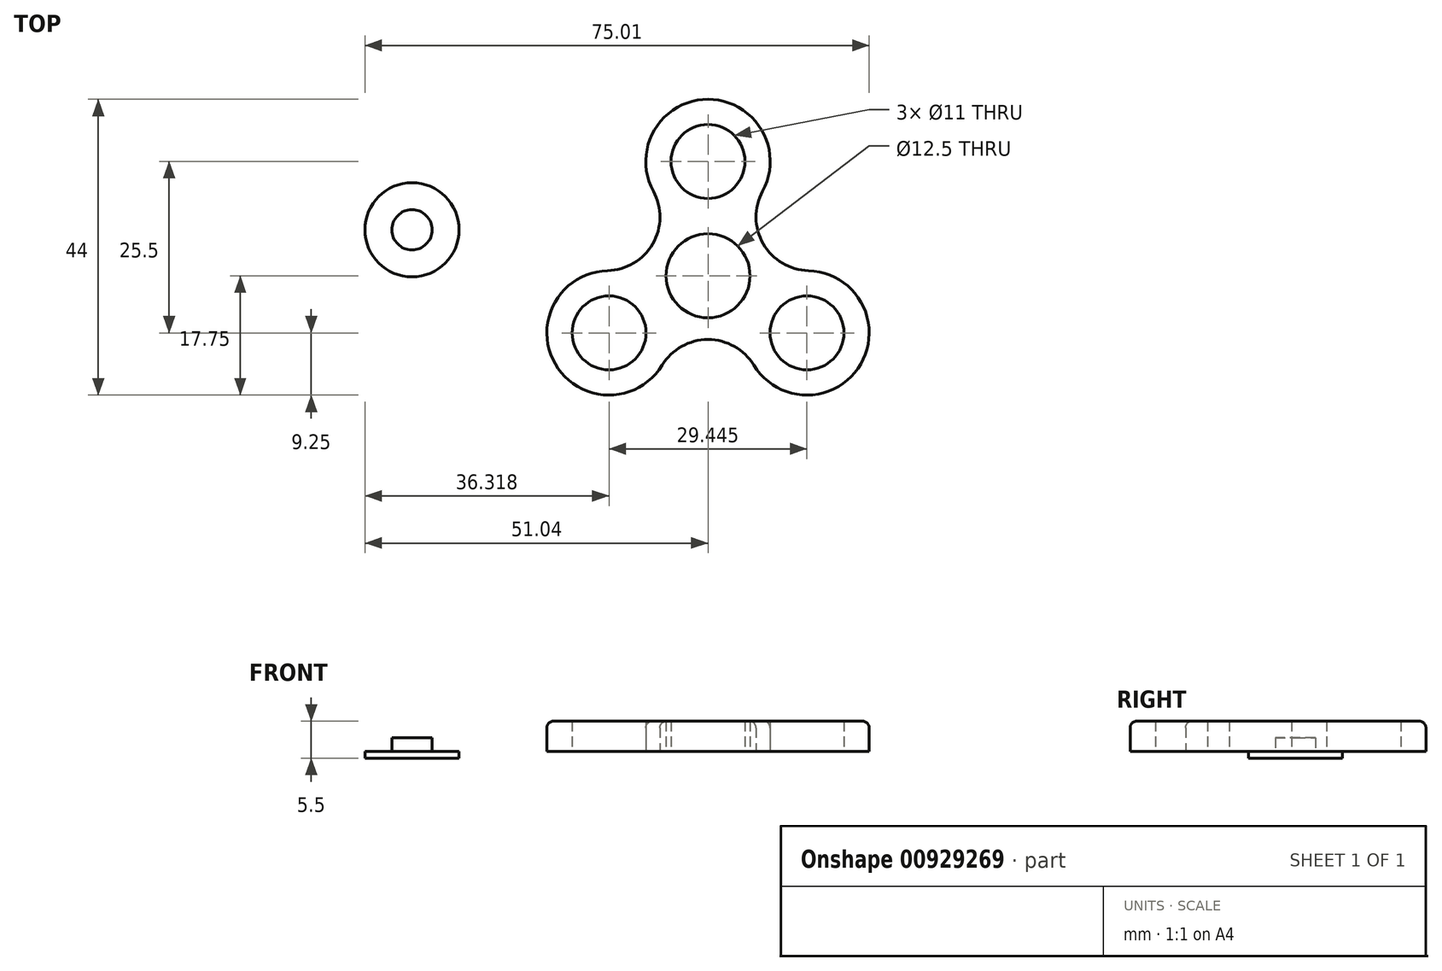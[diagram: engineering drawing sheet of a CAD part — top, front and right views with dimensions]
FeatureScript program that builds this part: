
annotation { "Feature Type Name" : "Feature", "Feature Type Description" : "" }
export const myFeature = defineFeature(function(context is Context, id is Id, definition is map)
    precondition{}
    {
        {
            var Q0;
            Q0=qCreatedBy(makeId("Top.planeOp"),FACE);
            var sketch = newSketch(context, id + "F0", { "sketchPlane" : qUnion([Q0])});
            skCircle(sketch, "E0", {"center": v(0, 0) * mm, "radius": 6.25 * mm});
            skLineSegment(sketch, "E1", {"start": v(0, 0) * mm, "end": v(0, 17) * mm});
            skLineSegment(sketch, "E2", {"start": v(0, 0) * mm, "end": v(14.72, -8.5) * mm});
            skLineSegment(sketch, "E3", {"start": v(0, 0) * mm, "end": v(-14.72, -8.5) * mm});
            skCircle(sketch, "E4", {"center": v(0, 17) * mm, "radius": 5.5 * mm});
            skCircle(sketch, "E5", {"center": v(-14.72, -8.5) * mm, "radius": 5.5 * mm});
            skCircle(sketch, "E6", {"center": v(14.72, -8.5) * mm, "radius": 5.5 * mm});
            skArc(sketch, "E7", {"start": v(8.12, 12.57) * mm, "mid": v(0, 26.25) * mm, "end": v(-8.12, 12.57) * mm});
            skArc(sketch, "E8", {"start": v(6.83, -13.32) * mm, "mid": v(22.73, -13.12) * mm, "end": v(14.95, 0.75) * mm});
            skArc(sketch, "E9", {"start": v(-14.95, 0.75) * mm, "mid": v(-22.73, -13.13) * mm, "end": v(-6.83, -13.32) * mm});
            skArc(sketch, "E10", {"start": v(-8.12, 12.57) * mm, "mid": v(-8.22, 4.74) * mm, "end": v(-14.95, 0.75) * mm});
            skArc(sketch, "E11", {"start": v(8.12, 12.57) * mm, "mid": v(8.22, 4.74) * mm, "end": v(14.95, 0.75) * mm});
            skArc(sketch, "E12", {"start": v(6.83, -13.32) * mm, "mid": v(0, -9.49) * mm, "end": v(-6.83, -13.32) * mm});
            skSolve(sketch);
        }
        {
            var Q0;
            Q0=makeQuery(id+"F0.imprint","IMPRINT",FACE,{"disambiguationData":[TD([[makeQuery(id+"F0.imprint","IMPRINT",EDGE,{"derivedFrom":sQuery(id+"F0.wireOp",EDGE,"E4")}),-1.0]])]});
            extrude(context, id + "F1", {"entities" : qUnion([Q0]), "depth" : 4.5 * mm, "offsetDistance" : 25 * mm});
        }
        {
            var Q0;
            Q0=qCreatedBy(makeId("Top.planeOp"),FACE);
            var sketch = newSketch(context, id + "F2", { "sketchPlane" : qUnion([Q0])});
            skCircle(sketch, "E13", {"center": v(-44.04, 6.83) * mm, "radius": 3 * mm});
            skCircle(sketch, "E14", {"center": v(-44.04, 6.83) * mm, "radius": 7 * mm});
            skSolve(sketch);
        }
        {
            var Q0;
            Q0=makeQuery(id+"F2.imprint","IMPRINT",FACE,{"disambiguationData":[TD([[makeQuery(id+"F2.imprint","IMPRINT",EDGE,{"derivedFrom":sQuery(id+"F2.wireOp",EDGE,"E13")}),1.0]])]});
            extrude(context, id + "F3", {"entities" : qUnion([Q0]), "depth" : 2 * mm, "offsetDistance" : 25 * mm});
        }
        {
            var Q0;
            Q0=makeQuery(id+"F2.imprint","IMPRINT",FACE,{"disambiguationData":[TD([[makeQuery(id+"F2.imprint","IMPRINT",EDGE,{"derivedFrom":sQuery(id+"F2.wireOp",EDGE,"E13")}),1.0]])]});
            var Q1;
            Q1=makeQuery(id+"F2.imprint","IMPRINT",FACE,{"disambiguationData":[TD([[makeQuery(id+"F2.imprint","IMPRINT",EDGE,{"derivedFrom":sQuery(id+"F2.wireOp",EDGE,"E13")}),-1.0]])]});
            extrude(context, id + "F4", {"entities" : qUnion([Q0, Q1]), "operationType" : NewBodyOperationType.ADD, "oppositeDirection" : true, "depth" : 1 * mm, "offsetDistance" : 25 * mm});
        }
        {
            var Q0;
            Q0=makeQuery(id+"F1.opExtrude","CAP_EDGE",EDGE,{"disambiguationData":[OSD([sQuery(id+"F0.wireOp",EDGE,"E12")])],"isStart":false});
            var Q1;
            Q1=makeQuery(id+"F1.opExtrude","CAP_EDGE",EDGE,{"disambiguationData":[OSD([sQuery(id+"F0.wireOp",EDGE,"E9")])],"isStart":false});
            var Q2;
            Q2=makeQuery(id+"F1.opExtrude","CAP_EDGE",EDGE,{"disambiguationData":[OSD([sQuery(id+"F0.wireOp",EDGE,"E10")])],"isStart":false});
            var Q3;
            Q3=makeQuery(id+"F1.opExtrude","CAP_EDGE",EDGE,{"disambiguationData":[OSD([sQuery(id+"F0.wireOp",EDGE,"E7")])],"isStart":false});
            var Q4;
            Q4=makeQuery(id+"F1.opExtrude","CAP_EDGE",EDGE,{"disambiguationData":[OSD([sQuery(id+"F0.wireOp",EDGE,"E11")])],"isStart":false});
            var Q5;
            Q5=makeQuery(id+"F1.opExtrude","CAP_EDGE",EDGE,{"disambiguationData":[OSD([sQuery(id+"F0.wireOp",EDGE,"E8")])],"isStart":false});
            fillet(context, id + "F5", {"entities" : qUnion([Q0, Q1, Q2, Q3, Q4, Q5]), "radius" : 1 * mm, "tangentPropagation" : true, "allowEdgeOverflow" : false});
        }
    });
